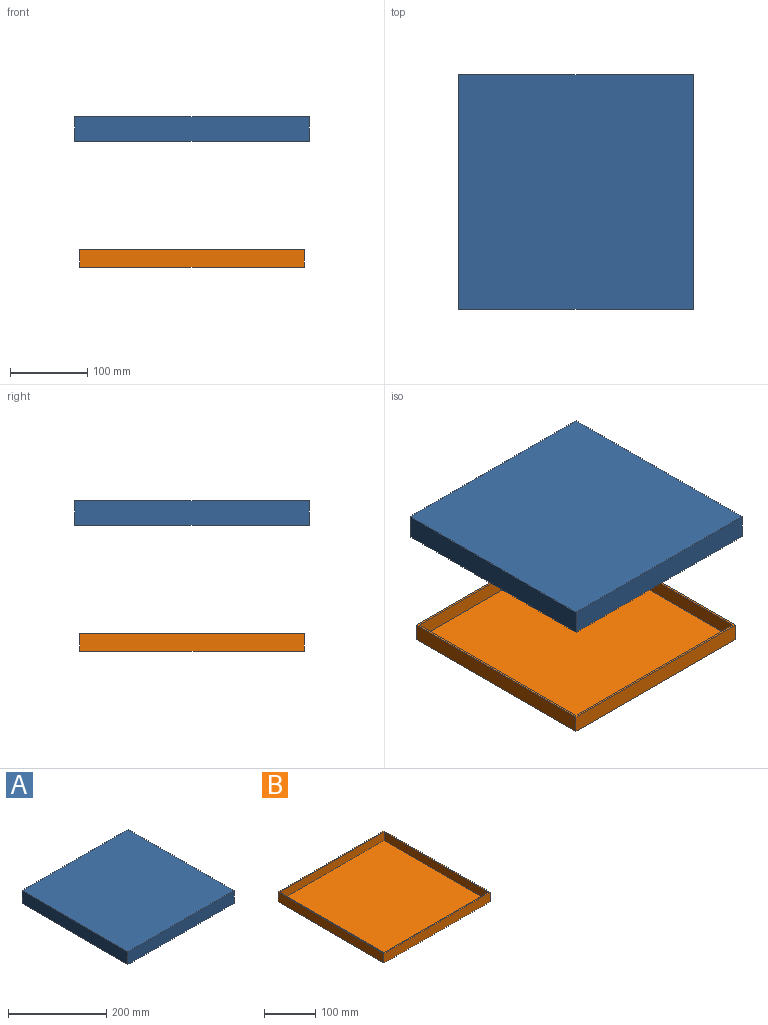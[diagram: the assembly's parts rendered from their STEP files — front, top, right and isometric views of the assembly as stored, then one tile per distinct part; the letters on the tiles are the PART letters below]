
ASSEMBLY  parts=2 mates=2
PART A: 11 faces, bbox 304.8x304.8x31.8 mm
  f0: plane 304.8x31.75mm, normal (-1,0,0), area 9677.4mm2, adj f1,f3,f4,f5
  f1: plane 304.8x31.75mm, normal (0,-1,0), area 9677.4mm2, adj f0,f2,f4,f5
  f2: plane 304.8x31.75mm, normal (1,0,0), area 9677.4mm2, adj f1,f3,f4,f5
  f3: plane 304.8x31.75mm, normal (0,1,0), area 9677.4mm2, adj f0,f2,f4,f5
  f4: plane 304.8x304.8mm, normal (0,0,1), area 92903mm2, adj f0,f1,f2,f3
  f5: plane 304.8x304.8mm, normal (0,0,-1), area 7580.6mm2, adj f0,f1,f2,f3,f6,f7,f8,f9
  f6: plane 292.1x25.4mm, normal (1,0,0), area 7419.3mm2, adj f5,f7,f9,f10
  f7: plane 292.1x25.4mm, normal (0,1,0), area 7419.3mm2, adj f5,f6,f8,f10
  f8: plane 292.1x25.4mm, normal (-1,0,0), area 7419.3mm2, adj f5,f7,f9,f10
  f9: plane 292.1x25.4mm, normal (0,-1,0), area 7419.3mm2, adj f5,f6,f8,f10
  f10: plane 292.1x292.1mm, normal (0,0,-1), area 85322.4mm2, adj f6,f7,f8,f9
PART B: 11 faces, bbox 292.1x292.1x22.9 mm
  f0: plane 292.1x22.86mm, normal (-1,0,0), area 6677.4mm2, adj f1,f3,f4,f5
  f1: plane 292.1x22.86mm, normal (0,-1,0), area 6677.4mm2, adj f0,f2,f4,f5
  f2: plane 292.1x22.86mm, normal (1,0,0), area 6677.4mm2, adj f1,f3,f4,f5
  f3: plane 292.1x22.86mm, normal (0,1,0), area 6677.4mm2, adj f0,f2,f4,f5
  f4: plane 292.1x292.1mm, normal (0,0,1), area 2941.9mm2, adj f0,f1,f2,f3,f6,f7,f8,f9
  f5: plane 292.1x292.1mm, normal (0,0,-1), area 85322.4mm2, adj f0,f1,f2,f3
  f6: plane 287.02x20.32mm, normal (1,0,0), area 5832.2mm2, adj f4,f7,f9,f10
  f7: plane 287.02x20.32mm, normal (0,1,0), area 5832.2mm2, adj f4,f6,f8,f10
  f8: plane 287.02x20.32mm, normal (-1,0,0), area 5832.2mm2, adj f4,f7,f9,f10
  f9: plane 287.02x20.32mm, normal (0,-1,0), area 5832.2mm2, adj f4,f6,f8,f10
  f10: plane 287.02x287.02mm, normal (0,0,1), area 82380.5mm2, adj f6,f7,f8,f9
PLACE A t=(18.48,30.09,181.24)mm
PLACE B t=(18.48,30.09,17.7)mm fixed
MATE planar B.f0 <-> A.f6  axis (-1,0,0) through (-127.57,30.09,29.13)mm
MATE planar B.f3 <-> A.f9  axis (0,1,0) through (18.48,176.14,29.13)mm
